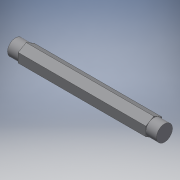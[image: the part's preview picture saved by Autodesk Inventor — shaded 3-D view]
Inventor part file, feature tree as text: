
AUTODESK INVENTOR PART (.ipt)
format: ipt  version: 2018 (Build 220112000, 112)  size: 123,904 bytes
history: native  units: in
note: dims shown in document units (in); Inventor stores cm internally (conversion verified against a paired STEP export)
features: extrude x3, sketch x3
ambient origin geometry x8: Origin, YZ Plane, XZ Plane, XY Plane, X Axis, Y Axis, Z Axis, Center Point
bodies: Solid1 (feature_tree)
feature tree (6):
  extrude  "Extrusion1"  Depth=1.35in TaperAngle=0.0deg
  extrude  "Extrusion2"  Depth=0.25in TaperAngle=0.0deg
  extrude  "Extrusion3"  Depth=0.25in TaperAngle=0.0deg
  sketch  "Sketch1"  dims[d0=0.1875in d1=1.35in d2=0.0in]
  sketch  "Sketch2"  dims[d3=0.1875in d4=0.25in d5=0.0in]
  sketch  "Sketch3"  dims[d6=0.1875in d7=0.25in d8=0.0in]
